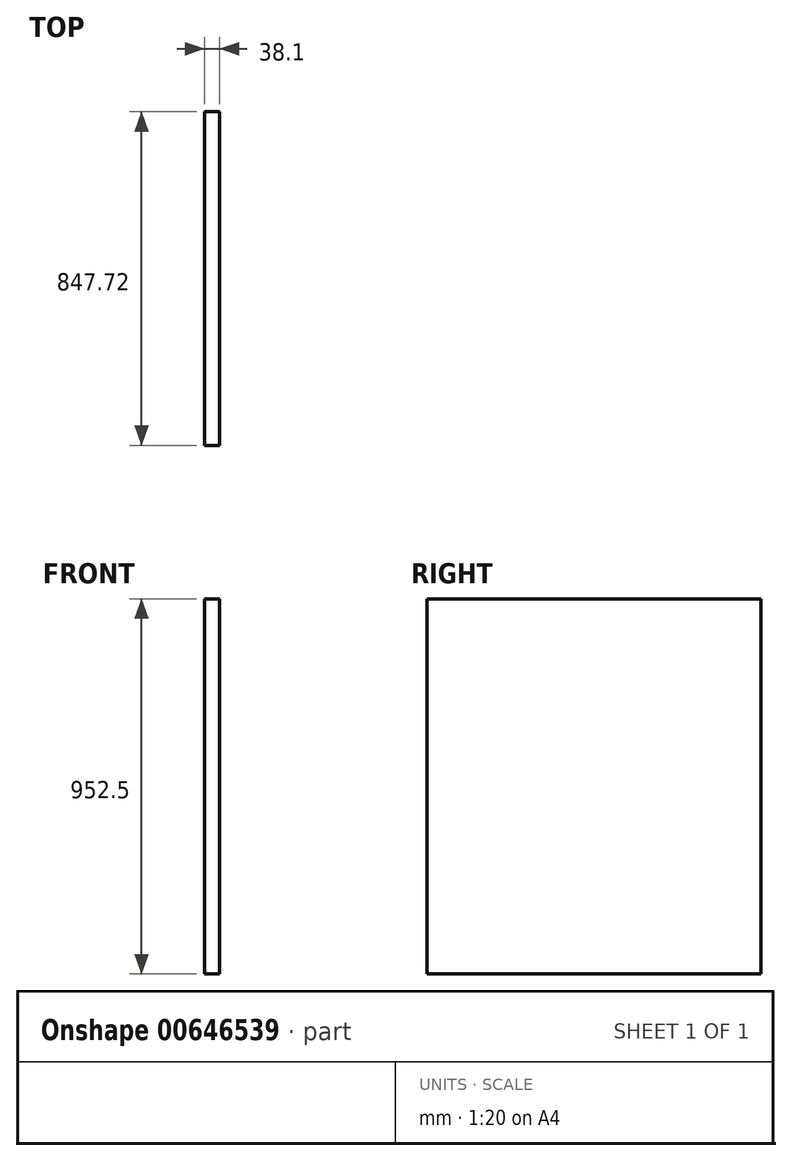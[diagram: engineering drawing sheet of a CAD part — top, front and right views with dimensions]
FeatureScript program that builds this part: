
annotation { "Feature Type Name" : "Feature", "Feature Type Description" : "" }
export const myFeature = defineFeature(function(context is Context, id is Id, definition is map)
    precondition{}
    {
        {
            var Q0;
            Q0=qCreatedBy(makeId("Right.planeOp"),FACE);
            var sketch = newSketch(context, id + "F0", { "sketchPlane" : qUnion([Q0])});
            skLineSegment(sketch, "E0.bottom", {"start": v(423.86, 476.25) * mm, "end": v(-423.86, 476.25) * mm});
            skLineSegment(sketch, "E0.top", {"start": v(423.86, -476.25) * mm, "end": v(-423.86, -476.25) * mm});
            skLineSegment(sketch, "E0.left", {"start": v(423.86, 476.25) * mm, "end": v(423.86, -476.25) * mm});
            skLineSegment(sketch, "E0.right", {"start": v(-423.86, 476.25) * mm, "end": v(-423.86, -476.25) * mm});
            skPoint(sketch, "E0.middle", {"position": v(0, 0) * mm});
            skSolve(sketch);
        }
        {
            var Q0;
            Q0=makeQuery(id+"F0.imprint","IMPRINT",FACE,{"disambiguationData":[TD([[makeQuery(id+"F0.imprint","IMPRINT",EDGE,{"derivedFrom":sQuery(id+"F0.wireOp",EDGE,"E0.bottom")}),1.0]])]});
            extrude(context, id + "F1", {"entities" : qUnion([Q0]), "depth" : 38.1 * mm, "offsetDistance" : 25.4 * mm});
        }
    });
